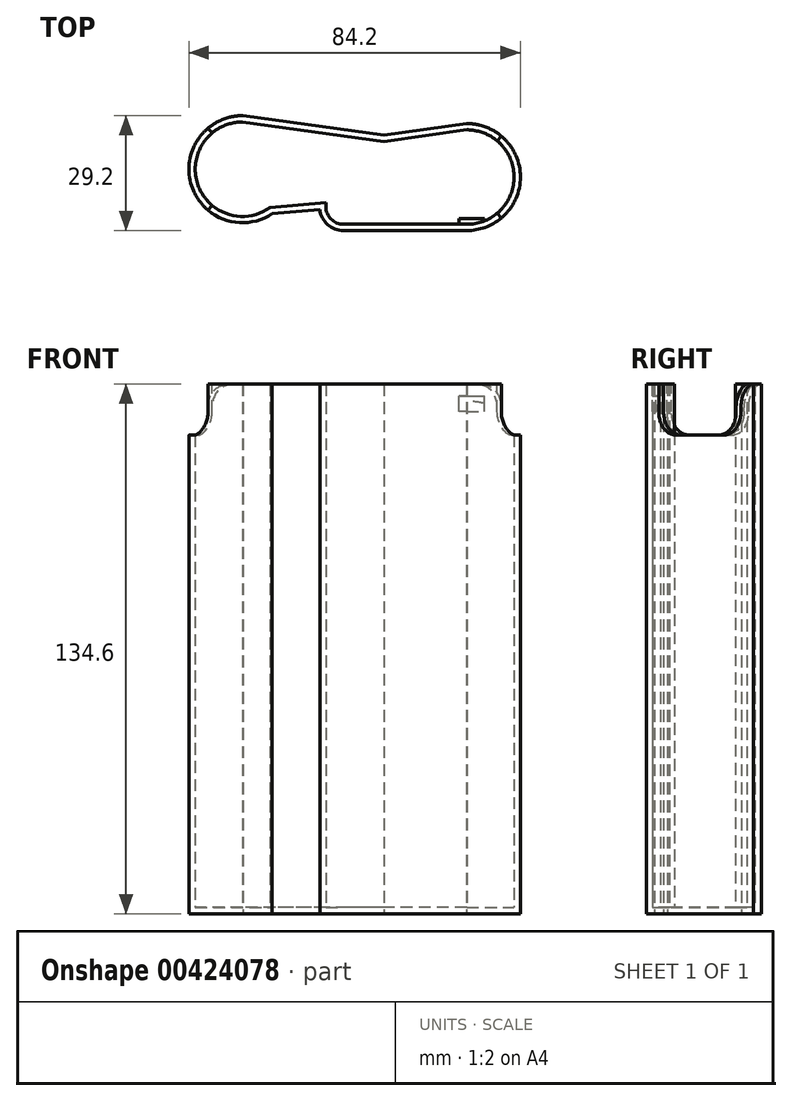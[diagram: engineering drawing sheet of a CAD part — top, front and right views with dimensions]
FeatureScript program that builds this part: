
annotation { "Feature Type Name" : "Feature", "Feature Type Description" : "" }
export const myFeature = defineFeature(function(context is Context, id is Id, definition is map)
    precondition{}
    {
        {
            var Q0;
            Q0=qCreatedBy(makeId("Top.planeOp"),FACE);
            var sketch = newSketch(context, id + "F0", { "sketchPlane" : qUnion([Q0])});
            skArc(sketch, "E0", {"start": v(36.27, -12) * mm, "mid": v(48.27, 0) * mm, "end": v(36.27, 12) * mm});
            skLineSegment(sketch, "E1", {"start": v(36.27, -12) * mm, "end": v(0.47, -12) * mm});
            skArc(sketch, "E2", {"start": v(-20.73, 14) * mm, "mid": v(-32.15, -1.68) * mm, "end": v(-13.73, -7.75) * mm});
            skLineSegment(sketch, "E3", {"start": v(-13.73, 24.59) * mm, "end": v(-13.73, -32.8) * mm, "construction": true});
            skLineSegment(sketch, "E4", {"start": v(-65.58, -6.5) * mm, "end": v(71.3, -6.5) * mm, "construction": true});
            skLineSegment(sketch, "E5", {"start": v(0.47, -6.5) * mm, "end": v(-13.73, -7.75) * mm});
            skLineSegment(sketch, "E6", {"start": v(4.97, 7.78) * mm, "end": v(4.97, -27.63) * mm, "construction": true});
            skLineSegment(sketch, "E7", {"start": v(0.47, -6.5) * mm, "end": v(0.47, -7.5) * mm});
            skArc(sketch, "E8", {"start": v(0.47, -7.5) * mm, "mid": v(1.79, -10.68) * mm, "end": v(4.97, -12) * mm});
            skLineSegment(sketch, "E9", {"start": v(15.27, 22.8) * mm, "end": v(15.27, -38.93) * mm, "construction": true});
            skLineSegment(sketch, "E10", {"start": v(10.13, 9) * mm, "end": v(19.4, 9) * mm, "construction": true});
            skLineSegment(sketch, "E11", {"start": v(36.27, 12) * mm, "end": v(15.27, 9) * mm});
            skLineSegment(sketch, "E12", {"start": v(15.27, 9) * mm, "end": v(-20.73, 14) * mm});
            skSolve(sketch);
        }
        {
            var Q0;
            {var subQ1=sQuery(id+"F0.wireOp",EDGE,"E0");Q0=makeQuery(id+"F0.imprint","IMPRINT",FACE,{"disambiguationData":[TD([[makeQuery(id+"F0.imprint","IMPRINT",EDGE,{"derivedFrom":subQ1}),1.0]])]});}
            extrude(context, id + "F1", {"entities" : qUnion([Q0]), "depth" : 133 * mm});
        }
        {
            var Q0;
            Q0=makeQuery(id+"F1.opExtrude","CAP_FACE",FACE,{"disambiguationData":[OSD([sQuery(id+"F0.wireOp",EDGE,"E0"),sQuery(id+"F0.wireOp",EDGE,"E1"),sQuery(id+"F0.wireOp",EDGE,"E2"),sQuery(id+"F0.wireOp",EDGE,"E5"),sQuery(id+"F0.wireOp",EDGE,"E7"),sQuery(id+"F0.wireOp",EDGE,"E8"),sQuery(id+"F0.wireOp",EDGE,"E11"),sQuery(id+"F0.wireOp",EDGE,"E12")])],"isStart":false});
            shell(context, id + "F2", {"entities" : qUnion([Q0]), "thickness" : 1.6 * mm, "oppositeDirection" : true});
        }
        {
            var Q0;
            Q0=makeQuery(id+"F1.opExtrude","CAP_FACE",FACE,{"disambiguationData":[OSD([sQuery(id+"F0.wireOp",EDGE,"E0"),sQuery(id+"F0.wireOp",EDGE,"E1"),sQuery(id+"F0.wireOp",EDGE,"E2"),sQuery(id+"F0.wireOp",EDGE,"E5"),sQuery(id+"F0.wireOp",EDGE,"E7"),sQuery(id+"F0.wireOp",EDGE,"E8"),sQuery(id+"F0.wireOp",EDGE,"E11"),sQuery(id+"F0.wireOp",EDGE,"E12")])],"isStart":false});
            var sketch = newSketch(context, id + "F3", { "sketchPlane" : qUnion([Q0])});
            skArc(sketch, "E13.0", {"start": v(36.27, -12) * mm, "mid": v(48.27, 0) * mm, "end": v(36.27, 12) * mm});
            skArc(sketch, "E13.1", {"start": v(36.27, -13.6) * mm, "mid": v(49.87, 0.06) * mm, "end": v(36.15, 13.6) * mm});
            skArc(sketch, "E13.2", {"start": v(-20.62, 15.6) * mm, "mid": v(-33.76, -1.9) * mm, "end": v(-13.17, -9.3) * mm});
            skArc(sketch, "E13.3", {"start": v(-20.73, 14) * mm, "mid": v(-32.15, -1.68) * mm, "end": v(-13.73, -7.75) * mm});
            skLineSegment(sketch, "E14", {"start": v(-20.73, 2) * mm, "end": v(-45.2, 2) * mm, "construction": true});
            skLineSegment(sketch, "E15", {"start": v(36.27, 0) * mm, "end": v(56.11, 0) * mm, "construction": true});
            skPoint(sketch, "E15.endSnap0", {"position": v(48.27, 0) * mm});
            skLineSegment(sketch, "E16", {"start": v(36.27, 0) * mm, "end": v(50.1, 16.48) * mm, "construction": true});
            skLineSegment(sketch, "E17", {"start": v(36.27, 0) * mm, "end": v(48.73, -14.85) * mm, "construction": true});
            skLineSegment(sketch, "E18", {"start": v(-20.73, 2) * mm, "end": v(-35.42, 19.5) * mm, "construction": true});
            skLineSegment(sketch, "E19", {"start": v(-20.73, 2) * mm, "end": v(-34.77, -14.74) * mm, "construction": true});
            skLineSegment(sketch, "E20", {"start": v(-28.44, 11.2) * mm, "end": v(-29.47, 12.42) * mm});
            skLineSegment(sketch, "E21", {"start": v(-28.44, -7.2) * mm, "end": v(-29.47, -8.42) * mm});
            skLineSegment(sketch, "E22", {"start": v(43.98, 9.2) * mm, "end": v(45.01, 10.42) * mm});
            skLineSegment(sketch, "E23", {"start": v(43.98, -9.2) * mm, "end": v(45.01, -10.42) * mm});
            skLineSegment(sketch, "E24.0", {"start": v(36.27, -13.6) * mm, "end": v(4.97, -13.6) * mm});
            skLineSegment(sketch, "E24.1", {"start": v(36.27, -12) * mm, "end": v(4.97, -12) * mm});
            skLineSegment(sketch, "E25", {"start": v(34.27, -12) * mm, "end": v(34.27, -10.5) * mm});
            skLineSegment(sketch, "E26", {"start": v(34.27, -10.5) * mm, "end": v(40.77, -10.5) * mm});
            skLineSegment(sketch, "E27", {"start": v(40.77, -10.5) * mm, "end": v(40.77, -11.12) * mm});
            skSolve(sketch);
        }
        {
            var Q0;
            {var subQ0=sQuery(id+"F3.wireOp",EDGE,"E22");Q0=makeQuery(id+"F3.imprint","IMPRINT",FACE,{"disambiguationData":[TD([[makeQuery(id+"F3.imprint","IMPRINT",EDGE,{"derivedFrom":subQ0}),-1.0]])]});}
            var Q1;
            {var subQ0=sQuery(id+"F3.wireOp",EDGE,"E20");Q1=makeQuery(id+"F3.imprint","IMPRINT",FACE,{"disambiguationData":[TD([[makeQuery(id+"F3.imprint","IMPRINT",EDGE,{"derivedFrom":subQ0}),1.0]])]});}
            extrude(context, id + "F4", {"entities" : qUnion([Q0, Q1]), "operationType" : NewBodyOperationType.REMOVE, "oppositeDirection" : true, "depth" : 13 * mm});
        }
        {
            var Q0;
            Q0=makeQuery(id+"F4.boolean.opBoolean","COPY",EDGE,{"derivedFrom":makeQuery(id+"F4.opExtrude","CAP_EDGE",EDGE,{"disambiguationData":[OSD([sQuery(id+"F3.wireOp",EDGE,"E22")])],"isStart":true})});
            var Q1;
            Q1=makeQuery(id+"F4.boolean.opBoolean","COPY",EDGE,{"derivedFrom":makeQuery(id+"F4.opExtrude","CAP_EDGE",EDGE,{"disambiguationData":[OSD([sQuery(id+"F3.wireOp",EDGE,"E22")])],"isStart":false})});
            var Q2;
            Q2=makeQuery(id+"F4.boolean.opBoolean","COPY",EDGE,{"derivedFrom":makeQuery(id+"F4.opExtrude","CAP_EDGE",EDGE,{"disambiguationData":[OSD([sQuery(id+"F3.wireOp",EDGE,"E20")])],"isStart":false})});
            var Q3;
            Q3=makeQuery(id+"F4.boolean.opBoolean","COPY",EDGE,{"derivedFrom":makeQuery(id+"F4.opExtrude","CAP_EDGE",EDGE,{"disambiguationData":[OSD([sQuery(id+"F3.wireOp",EDGE,"E20")])],"isStart":true})});
            var Q4;
            Q4=makeQuery(id+"F4.boolean.opBoolean","COPY",EDGE,{"derivedFrom":makeQuery(id+"F4.opExtrude","CAP_EDGE",EDGE,{"disambiguationData":[OSD([sQuery(id+"F3.wireOp",EDGE,"E23")])],"isStart":true})});
            var Q5;
            Q5=makeQuery(id+"F4.boolean.opBoolean","COPY",EDGE,{"derivedFrom":makeQuery(id+"F4.opExtrude","CAP_EDGE",EDGE,{"disambiguationData":[OSD([sQuery(id+"F3.wireOp",EDGE,"E21")])],"isStart":true})});
            var Q6;
            Q6=makeQuery(id+"F4.boolean.opBoolean","COPY",EDGE,{"derivedFrom":makeQuery(id+"F4.opExtrude","CAP_EDGE",EDGE,{"disambiguationData":[OSD([sQuery(id+"F3.wireOp",EDGE,"E21")])],"isStart":false})});
            var Q7;
            Q7=makeQuery(id+"F4.boolean.opBoolean","COPY",EDGE,{"derivedFrom":makeQuery(id+"F4.opExtrude","CAP_EDGE",EDGE,{"disambiguationData":[OSD([sQuery(id+"F3.wireOp",EDGE,"E23")])],"isStart":false})});
            fillet(context, id + "F5", {"entities" : qUnion([Q0, Q1, Q2, Q3, Q4, Q5, Q6, Q7]), "radius" : 6 * mm, "tangentPropagation" : true, "allowEdgeOverflow" : false});
        }
        {
            var Q0;
            {var subQ3=sQuery(id+"F3.wireOp",EDGE,"E25");Q0=makeQuery(id+"F3.imprint","IMPRINT",FACE,{"disambiguationData":[TD([[makeQuery(id+"F3.imprint","IMPRINT",EDGE,{"derivedFrom":subQ3}),-1.0]])]});}
            extrude(context, id + "F6", {"entities" : qUnion([Q0]), "operationType" : NewBodyOperationType.ADD, "oppositeDirection" : true, "depth" : 7 * mm});
        }
        {
            var Q0;
            {var subQ3=sQuery(id+"F3.wireOp",EDGE,"E25");Q0=makeQuery(id+"F3.imprint","IMPRINT",FACE,{"disambiguationData":[TD([[makeQuery(id+"F3.imprint","IMPRINT",EDGE,{"derivedFrom":subQ3}),-1.0]])]});}
            extrude(context, id + "F7", {"entities" : qUnion([Q0]), "operationType" : NewBodyOperationType.REMOVE, "oppositeDirection" : true, "depth" : 3 * mm});
        }
        {
            var Q0;
            Q0=makeQuery(id+"F6.opExtrude","CAP_EDGE",EDGE,{"disambiguationData":[OSD([sQuery(id+"F3.wireOp",EDGE,"E26")])],"isStart":false});
            var Q1;
            Q1=makeQuery(id+"F7.boolean.opBoolean","COPY",EDGE,{"derivedFrom":makeQuery(id+"F7.opExtrude","CAP_EDGE",EDGE,{"disambiguationData":[OSD([sQuery(id+"F3.wireOp",EDGE,"E26")])],"isStart":false})});
            fillet(context, id + "F8", {"entities" : qUnion([Q0, Q1]), "radius" : 3 * mm, "tangentPropagation" : true, "allowEdgeOverflow" : false});
        }
    });
